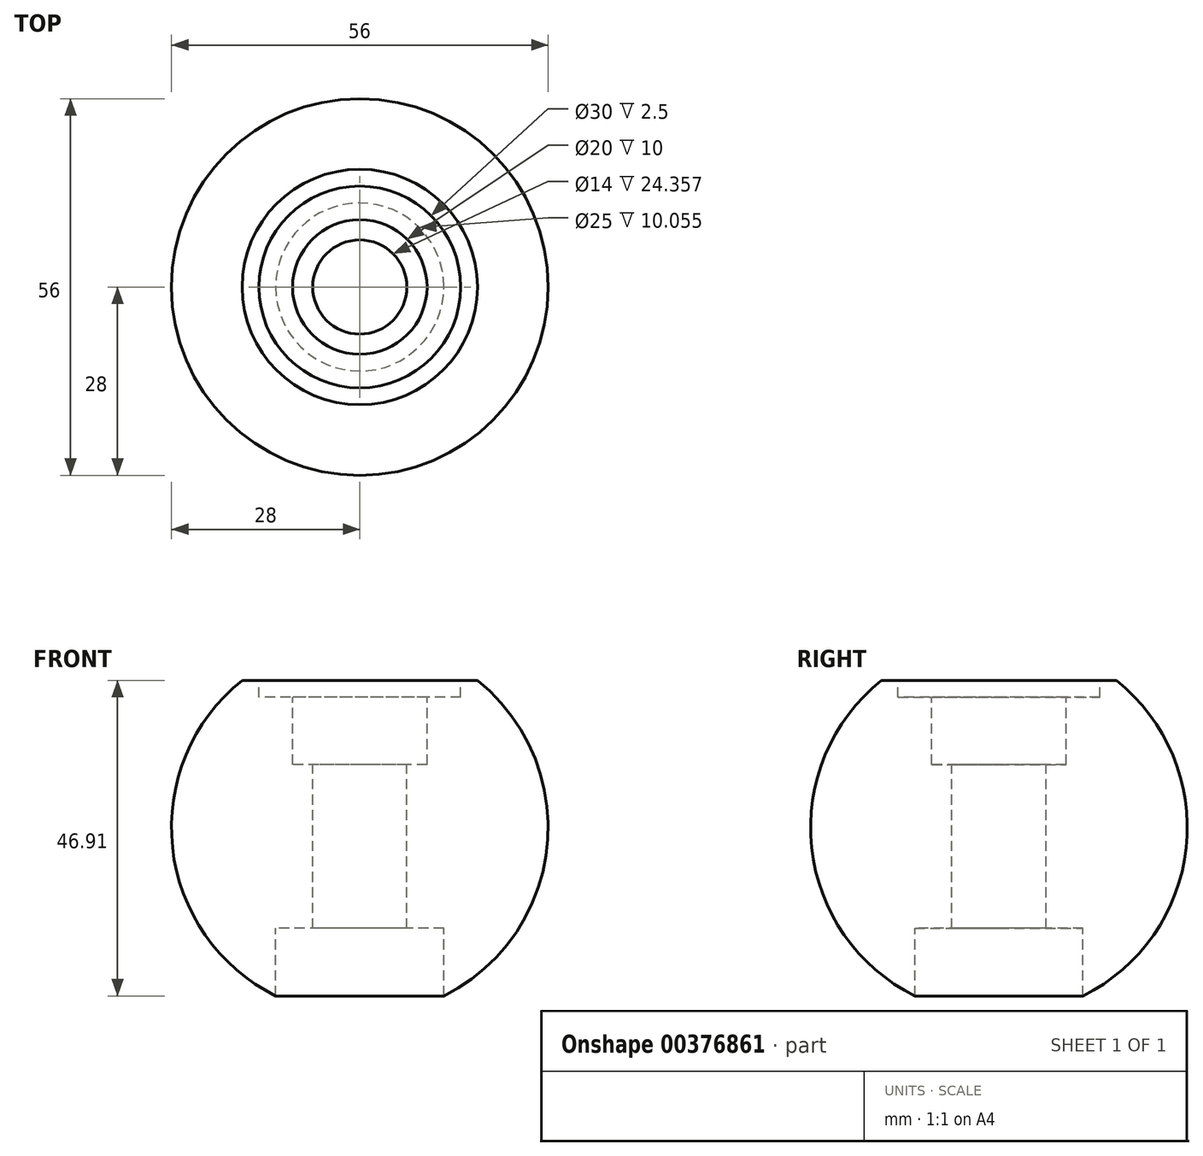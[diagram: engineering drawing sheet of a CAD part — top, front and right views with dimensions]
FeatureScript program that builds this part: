
annotation { "Feature Type Name" : "Feature", "Feature Type Description" : "" }
export const myFeature = defineFeature(function(context is Context, id is Id, definition is map)
    precondition{}
    {
        {
            var Q0;
            Q0=qCreatedBy(makeId("Front.planeOp"),FACE);
            var sketch = newSketch(context, id + "F0", { "sketchPlane" : qUnion([Q0])});
            skArc(sketch, "E0", {"start": v(-17.5, 21.86) * mm, "mid": v(-26.42, -9.27) * mm, "end": v(0, -28) * mm});
            skLineSegment(sketch, "E1", {"start": v(0, 21.86) * mm, "end": v(0, -28) * mm});
            skLineSegment(sketch, "E2", {"start": v(0, 21.86) * mm, "end": v(-17.5, 21.86) * mm});
            skPoint(sketch, "E3.orphan", {"position": v(0, 28) * mm});
            skSolve(sketch);
        }
        {
            var Q0;
            Q0=makeQuery(id+"F0.imprint","IMPRINT",FACE,{"disambiguationData":[TD([[makeQuery(id+"F0.imprint","IMPRINT",EDGE,{"derivedFrom":sQuery(id+"F0.wireOp",EDGE,"E0")}),1.0]])]});
            var Q1;
            Q1=sQuery(id+"F0.wireOp",EDGE,"E1");
            revolve(context, id + "F1", {"entities" : qUnion([Q0]), "axis" : qUnion([Q1]), "revolveType" : RevolveType.FULL});
        }
        {
            var Q0;
            Q0=makeQuery(id+"F1.opRevolve","SWEPT_FACE",FACE,{"disambiguationData":[OSD([sQuery(id+"F0.wireOp",EDGE,"E2")])]});
            var sketch = newSketch(context, id + "F2", { "sketchPlane" : qUnion([Q0])});
            skCircle(sketch, "E4", {"center": v(0, 0) * mm, "radius": 15 * mm});
            skSolve(sketch);
        }
        {
            var Q0;
            Q0 = qSketchRegion(id + "F2", true);
            extrude(context, id + "F3", {"entities" : qUnion([Q0]), "operationType" : NewBodyOperationType.REMOVE, "oppositeDirection" : true, "depth" : 2.5 * mm});
        }
        {
            var Q0;
            Q0=makeQuery(id+"F3.boolean.opBoolean","COPY",FACE,{"derivedFrom":makeQuery(id+"F3.opExtrude","CAP_FACE",FACE,{"disambiguationData":[OSD([sQuery(id+"F2.wireOp",EDGE,"E4")])],"isStart":false})});
            var sketch = newSketch(context, id + "F4", { "sketchPlane" : qUnion([Q0])});
            skCircle(sketch, "E5", {"center": v(0, 0) * mm, "radius": 10 * mm});
            skSolve(sketch);
        }
        {
            var Q0;
            Q0 = qSketchRegion(id + "F4", true);
            extrude(context, id + "F5", {"entities" : qUnion([Q0]), "operationType" : NewBodyOperationType.REMOVE, "oppositeDirection" : true, "depth" : 10 * mm});
        }
        {
            var Q0;
            Q0=makeQuery(id+"F5.boolean.opBoolean","COPY",FACE,{"derivedFrom":makeQuery(id+"F5.opExtrude","CAP_FACE",FACE,{"disambiguationData":[OSD([sQuery(id+"F4.wireOp",EDGE,"E5")])],"isStart":false})});
            var sketch = newSketch(context, id + "F6", { "sketchPlane" : qUnion([Q0])});
            skCircle(sketch, "E6", {"center": v(0, 0) * mm, "radius": 7 * mm});
            skSolve(sketch);
        }
        {
            var Q0;
            Q0 = qSketchRegion(id + "F6", true);
            extrude(context, id + "F7", {"entities" : qUnion([Q0]), "operationType" : NewBodyOperationType.REMOVE, "endBound" : BoundingType.THROUGH_ALL, "oppositeDirection" : true, "depth" : 25 * mm});
        }
        {
            var Q0;
            Q0=qCreatedBy(makeId("Top.planeOp"),FACE);
            cPlane(context, id + "F8", {"entities" : qUnion([Q0]), "cplaneType" : CPlaneType.OFFSET, "offset" : 15 * mm, "oppositeDirection" : true, "width" : 150 * mm, "height" : 150 * mm});
        }
        {
            var Q0;
            Q0=qCreatedBy(id+"F8.planeOp",FACE);
            var sketch = newSketch(context, id + "F9", { "sketchPlane" : qUnion([Q0])});
            skCircle(sketch, "E7", {"center": v(0, 0) * mm, "radius": 12.5 * mm});
            skSolve(sketch);
        }
        {
            var Q0;
            Q0 = qSketchRegion(id + "F9", true);
            extrude(context, id + "F10", {"entities" : qUnion([Q0]), "operationType" : NewBodyOperationType.REMOVE, "oppositeDirection" : true, "depth" : 25 * mm});
        }
    });
